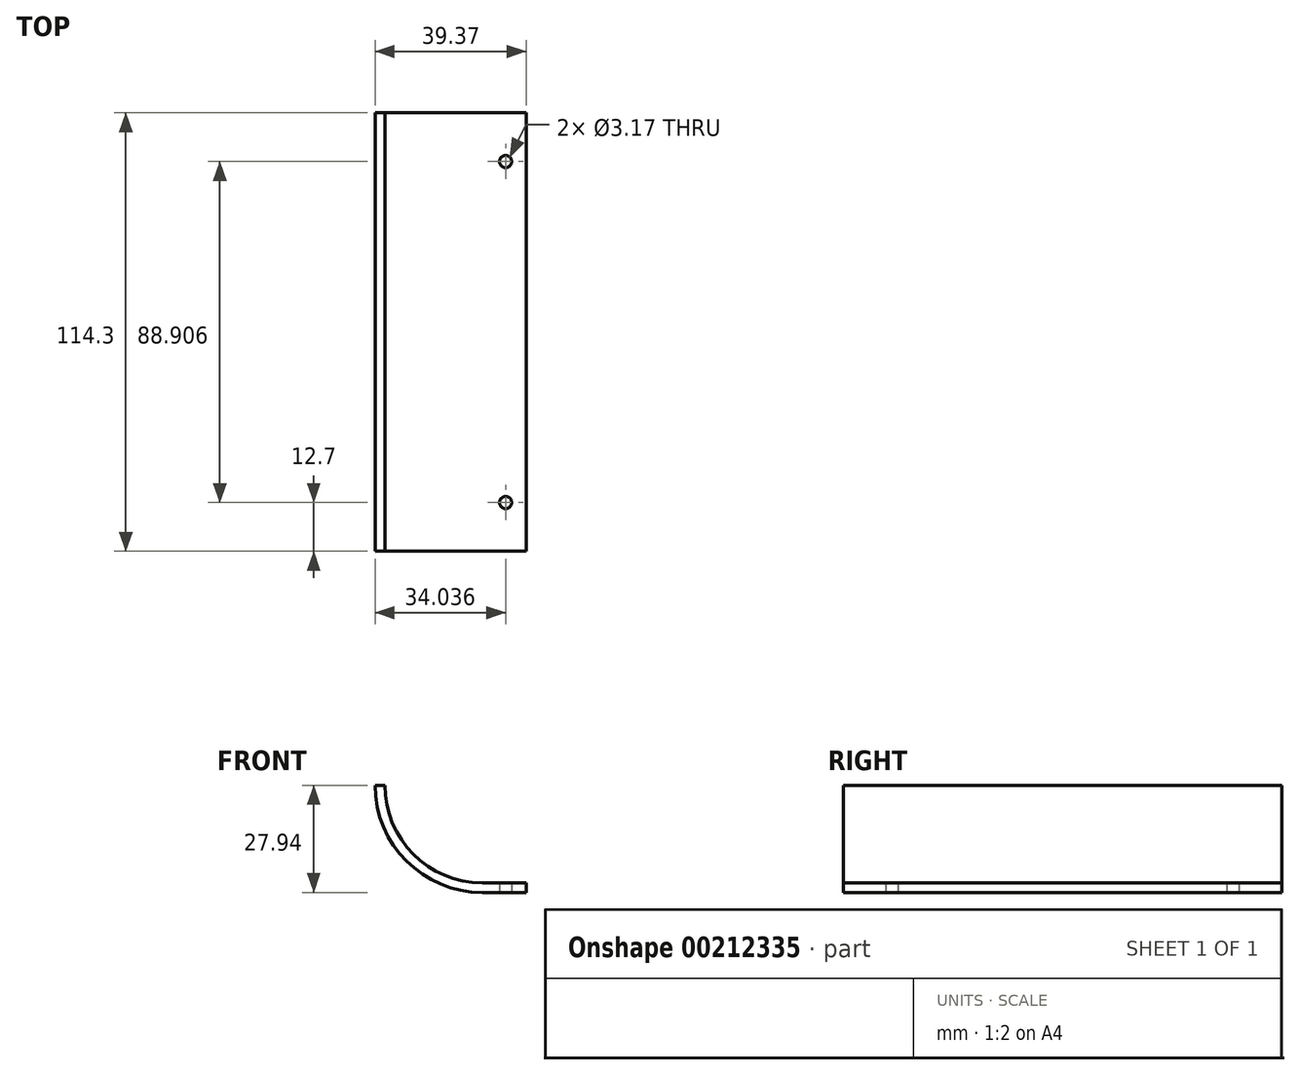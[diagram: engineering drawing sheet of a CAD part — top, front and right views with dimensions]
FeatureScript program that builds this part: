
annotation { "Feature Type Name" : "Feature", "Feature Type Description" : "" }
export const myFeature = defineFeature(function(context is Context, id is Id, definition is map)
    precondition{}
    {
        {
            var Q0;
            Q0=qCreatedBy(makeId("Front.planeOp"),FACE);
            var sketch = newSketch(context, id + "F0", { "sketchPlane" : qUnion([Q0])});
            skArc(sketch, "E0", {"start": v(-25.4, 0) * mm, "mid": v(-17.96, -17.96) * mm, "end": v(0, -25.4) * mm});
            skLineSegment(sketch, "E1", {"start": v(0, -25.4) * mm, "end": v(11.43, -25.4) * mm});
            skLineSegment(sketch, "E2", {"start": v(-25.4, 0) * mm, "end": v(-27.94, 0) * mm});
            skLineSegment(sketch, "E3", {"start": v(11.43, -25.4) * mm, "end": v(11.43, -27.94) * mm});
            skArc(sketch, "E4", {"start": v(-27.94, 0) * mm, "mid": v(-19.76, -19.76) * mm, "end": v(0, -27.94) * mm});
            skLineSegment(sketch, "E5", {"start": v(11.43, -27.94) * mm, "end": v(0, -27.94) * mm});
            skSolve(sketch);
        }
        {
            var Q0;
            Q0 = qSketchRegion(id + "F0", true);
            extrude(context, id + "F1", {"entities" : qUnion([Q0]), "depth" : 114.3 * mm});
        }
        {
            var Q0;
            Q0=makeQuery(id+"F1.opExtrude","SWEPT_FACE",FACE,{"disambiguationData":[OSD([sQuery(id+"F0.wireOp",EDGE,"E5")])]});
            var sketch = newSketch(context, id + "F2", { "sketchPlane" : qUnion([Q0])});
            skCircle(sketch, "E6", {"center": v(6.1, 12.7) * mm, "radius": 1.59 * mm});
            skCircle(sketch, "E7", {"center": v(6.1, 101.6) * mm, "radius": 1.59 * mm});
            skSolve(sketch);
        }
        {
            var Q0;
            Q0 = qSketchRegion(id + "F2", true);
            extrude(context, id + "F3", {"entities" : qUnion([Q0]), "operationType" : NewBodyOperationType.REMOVE, "endBound" : BoundingType.THROUGH_ALL, "oppositeDirection" : true, "depth" : 25.4 * mm});
        }
    });
